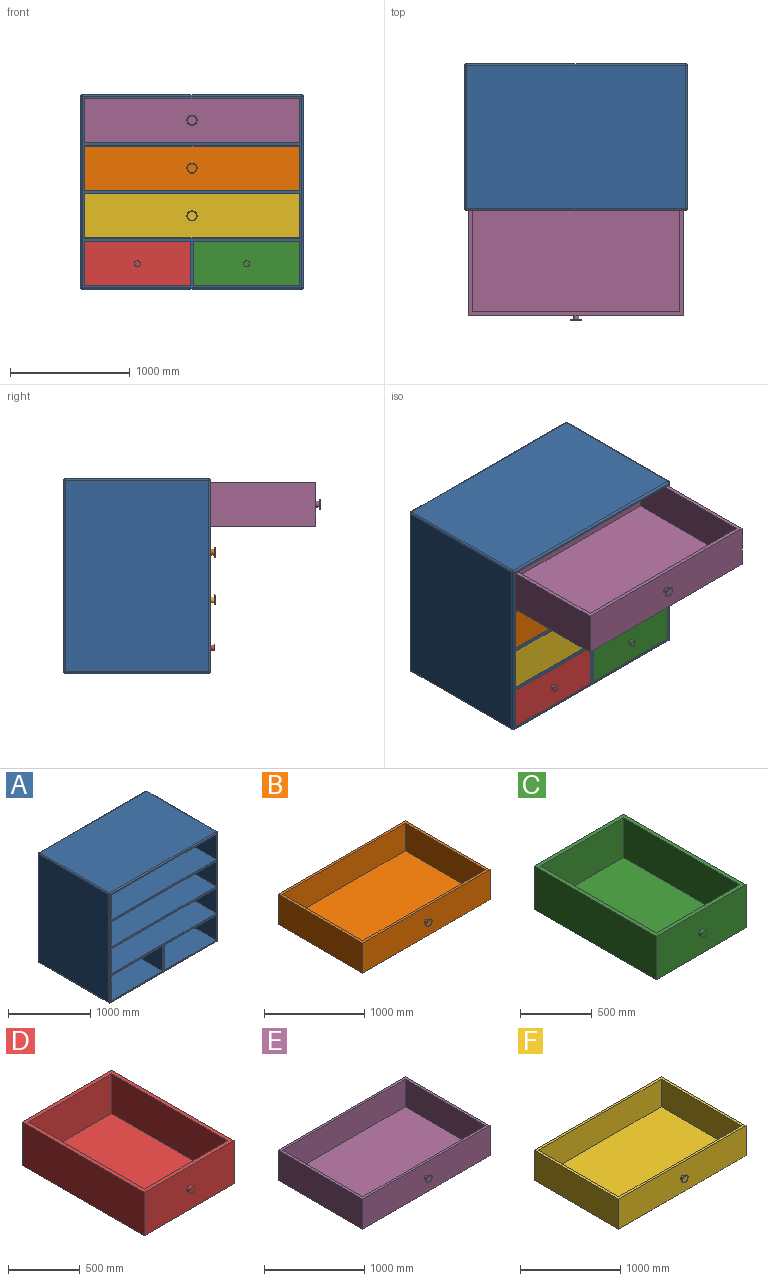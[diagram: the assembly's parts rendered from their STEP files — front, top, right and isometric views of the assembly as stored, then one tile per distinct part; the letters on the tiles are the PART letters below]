
ASSEMBLY  parts=6 mates=5
PART A: 51 faces, bbox 1860x1230x1630 mm
  f0: plane 885x370mm, normal (0,-1,0), area 327450mm2, adj f15,f21,f28,f29
  f1: plane 1200x885mm, normal (0,0,1), area 1062000mm2, adj f3,f12,f20,f30
  f2: plane 1200x885mm, normal (0,0,-1), area 1062000mm2, adj f3,f12,f20,f30
  f3: plane 1200x370mm, normal (-1,0,0), area 444000mm2, adj f1,f2,f12,f20
  f4: plane 1200x370mm, normal (1,0,0), area 444000mm2, adj f5,f12,f23,f27
  f5: plane 1800x370mm, normal (0,-1,0), area 666000mm2, adj f4,f10,f23,f27
  f6: plane 1200x370mm, normal (1,0,0), area 444000mm2, adj f7,f12,f14,f25
  f7: plane 1800x370mm, normal (0,-1,0), area 666000mm2, adj f6,f14,f17,f25
  f8: plane 1200x370mm, normal (-1,0,0), area 444000mm2, adj f11,f12,f24,f26
  f9: plane 1200x370mm, normal (1,0,0), area 444000mm2, adj f11,f12,f24,f26
  f10: plane 1200x370mm, normal (-1,0,0), area 444000mm2, adj f5,f12,f23,f27
  f11: plane 1800x370mm, normal (0,-1,0), area 666000mm2, adj f8,f9,f24,f26
  f12: plane 1830x1600mm, normal (0,-1,0), area 275100mm2, adj f1,f2,f3,f4,f6,f8,f9,f10
  f13: plane 1830x1200mm, normal (0,0,1), area 2196000mm2, adj f31,f35,f36,f37
  f14: plane 1800x1200mm, normal (0,0,-1), area 2160000mm2, adj f6,f7,f12,f17
  f15: plane 1200x370mm, normal (1,0,0), area 444000mm2, adj f0,f12,f21,f28
  f16: plane 1600x1200mm, normal (-1,0,0), area 1920000mm2, adj f37,f38,f46,f47
  f17: plane 1200x370mm, normal (-1,0,0), area 444000mm2, adj f7,f12,f14,f25
  f18: plane 1600x1200mm, normal (1,0,0), area 1920000mm2, adj f34,f35,f44,f45
  f19: plane 1830x1600mm, normal (0,1,0), area 2928000mm2, adj f36,f45,f46,f50
  f20: plane 885x370mm, normal (0,-1,0), area 327450mm2, adj f1,f2,f3,f30
  f21: plane 1200x885mm, normal (0,0,1), area 1062000mm2, adj f0,f12,f15,f29
  f22: plane 1830x1200mm, normal (0,0,-1), area 2196000mm2, adj f39,f44,f47,f50
  f23: plane 1800x1200mm, normal (0,0,-1), area 2160000mm2, adj f4,f5,f10,f12
  f24: plane 1800x1200mm, normal (0,0,1), area 2160000mm2, adj f8,f9,f11,f12
  f25: plane 1800x1200mm, normal (0,0,1), area 2160000mm2, adj f6,f7,f12,f17
  f26: plane 1800x1200mm, normal (0,0,-1), area 2160000mm2, adj f8,f9,f11,f12
  f27: plane 1800x1200mm, normal (0,0,1), area 2160000mm2, adj f4,f5,f10,f12
  f28: plane 1200x885mm, normal (0,0,-1), area 1062000mm2, adj f0,f12,f15,f29
  f29: plane 1200x370mm, normal (-1,0,0), area 444000mm2, adj f0,f12,f21,f28
  f30: plane 1200x370mm, normal (1,0,0), area 444000mm2, adj f1,f2,f12,f20
  f31: cylinder r=15mm len=1830mm, axis (-1,0,0), area 43118.4mm2, adj f12,f13,f32,f33
  f32: sphere r=15mm, area 353.4mm2, adj f31,f34,f35
  f33: sphere r=15mm, area 353.4mm2, adj f31,f37,f38
  f34: cylinder r=15mm len=1600mm, axis (0,0,-1), area 37699.1mm2, adj f12,f18,f32,f40
  f35: cylinder r=15mm len=1200mm, axis (0,-1,0), area 28274.3mm2, adj f13,f18,f32,f41
  f36: cylinder r=15mm len=1830mm, axis (-1,0,0), area 43118.4mm2, adj f13,f19,f41,f42
  f37: cylinder r=15mm len=1200mm, axis (0,-1,0), area 28274.3mm2, adj f13,f16,f33,f42
  f38: cylinder r=15mm len=1600mm, axis (0,0,-1), area 37699.1mm2, adj f12,f16,f33,f43
  f39: cylinder r=15mm len=1830mm, axis (1,0,0), area 43118.4mm2, adj f12,f22,f40,f43
  f40: sphere r=15mm, area 353.4mm2, adj f34,f39,f44
  f41: sphere r=15mm, area 353.4mm2, adj f35,f36,f45
  f42: sphere r=15mm, area 353.4mm2, adj f36,f37,f46
  f43: sphere r=15mm, area 353.4mm2, adj f38,f39,f47
  f44: cylinder r=15mm len=1200mm, axis (0,-1,0), area 28274.3mm2, adj f18,f22,f40,f48
  f45: cylinder r=15mm len=1600mm, axis (0,0,-1), area 37699.1mm2, adj f18,f19,f41,f48
  f46: cylinder r=15mm len=1600mm, axis (0,0,-1), area 37699.1mm2, adj f16,f19,f42,f49
  f47: cylinder r=15mm len=1200mm, axis (0,-1,0), area 28274.3mm2, adj f16,f22,f43,f49
  f48: sphere r=15mm, area 353.4mm2, adj f44,f45,f50
  f49: sphere r=15mm, area 353.4mm2, adj f46,f47,f50
  f50: cylinder r=15mm len=1830mm, axis (-1,0,0), area 43118.4mm2, adj f19,f22,f48,f49
PART B: 15 faces, bbox 1798x1240x368 mm
  f0: plane 1738x1140mm, normal (0,0,1), area 1981320mm2, adj f1,f2,f3,f10
  f1: plane 1140x338mm, normal (1,0,0), area 385320mm2, adj f0,f3,f5,f10
  f2: plane 1140x338mm, normal (-1,0,0), area 385320mm2, adj f0,f3,f5,f10
  f3: plane 1738x338mm, normal (0,-1,0), area 587444mm2, adj f0,f1,f2,f5
  f4: plane 1200x368mm, normal (1,0,0), area 441600mm2, adj f5,f7,f8,f9
  f5: plane 1798x1200mm, normal (0,0,1), area 176280mm2, adj f1,f2,f3,f4,f6,f8,f9,f10
  f6: plane 1200x368mm, normal (-1,0,0), area 441600mm2, adj f5,f7,f8,f9
  f7: plane 1798x1200mm, normal (0,0,-1), area 2157600mm2, adj f4,f6,f8,f9
  f8: plane 1798x368mm, normal (0,1,0), area 661664mm2, adj f4,f5,f6,f7
  f9: plane 1798x368mm, normal (0,-1,0), area 659700.5mm2, adj f4,f5,f6,f7,f11
  f10: plane 1738x338mm, normal (0,1,0), area 587444mm2, adj f0,f1,f2,f5
  f11: cylinder r=25mm len=50mm, axis (0,1,0), area 4712.4mm2, adj f9,f13
  f12: plane 75.11x75.11mm, normal (0,-1,0), area 4431.2mm2, adj f14
  f13: plane 75.11x75.11mm, normal (0,1,0), area 2467.7mm2, adj f11,f14
  f14: torus R=37.56mm, axis (0,-1,0), area 4020.8mm2, adj f12,f13
PART C: 13 faces, bbox 883x1230x368 mm
  f0: plane 1140x823mm, normal (0,0,1), area 938220mm2, adj f1,f8,f9,f10
  f1: plane 1140x338mm, normal (-1,0,0), area 385320mm2, adj f0,f7,f8,f10
  f2: plane 883x368mm, normal (0,-1,0), area 322980.5mm2, adj f3,f5,f6,f7,f11
  f3: plane 1200x368mm, normal (-1,0,0), area 441600mm2, adj f2,f4,f6,f7
  f4: plane 883x368mm, normal (0,1,0), area 324944mm2, adj f3,f5,f6,f7
  f5: plane 1200x368mm, normal (1,0,0), area 441600mm2, adj f2,f4,f6,f7
  f6: plane 1200x883mm, normal (0,0,-1), area 1059600mm2, adj f2,f3,f4,f5
  f7: plane 1200x883mm, normal (0,0,1), area 121380mm2, adj f1,f2,f3,f4,f5,f8,f9,f10
  f8: plane 823x338mm, normal (0,-1,0), area 278174mm2, adj f0,f1,f7,f9
  f9: plane 1140x338mm, normal (1,0,0), area 385320mm2, adj f0,f7,f8,f10
  f10: plane 823x338mm, normal (0,1,0), area 278174mm2, adj f0,f1,f7,f9
  f11: cylinder r=25mm len=50mm, axis (0,1,0), area 4712.4mm2, adj f2,f12
  f12: plane 50x50mm, normal (0,-1,0), area 1963.5mm2, adj f11
PART D: 13 faces, bbox 883x1230x368 mm
  f0: plane 1140x823mm, normal (0,0,1), area 938220mm2, adj f1,f8,f9,f10
  f1: plane 1140x338mm, normal (1,0,0), area 385320mm2, adj f0,f7,f8,f10
  f2: plane 883x368mm, normal (0,-1,0), area 322980.5mm2, adj f3,f5,f6,f7,f11
  f3: plane 1200x368mm, normal (1,0,0), area 441600mm2, adj f2,f4,f6,f7
  f4: plane 883x368mm, normal (0,1,0), area 324944mm2, adj f3,f5,f6,f7
  f5: plane 1200x368mm, normal (-1,0,0), area 441600mm2, adj f2,f4,f6,f7
  f6: plane 1200x883mm, normal (0,0,-1), area 1059600mm2, adj f2,f3,f4,f5
  f7: plane 1200x883mm, normal (0,0,1), area 121380mm2, adj f1,f2,f3,f4,f5,f8,f9,f10
  f8: plane 823x338mm, normal (0,-1,0), area 278174mm2, adj f0,f1,f7,f9
  f9: plane 1140x338mm, normal (-1,0,0), area 385320mm2, adj f0,f7,f8,f10
  f10: plane 823x338mm, normal (0,1,0), area 278174mm2, adj f0,f1,f7,f9
  f11: cylinder r=25mm len=50mm, axis (0,1,0), area 4712.4mm2, adj f2,f12
  f12: plane 50x50mm, normal (0,-1,0), area 1963.5mm2, adj f11
PART E: 15 faces, bbox 1798x1240x368 mm
  f0: plane 1738x1140mm, normal (0,0,1), area 1981320mm2, adj f1,f2,f3,f10
  f1: plane 1140x338mm, normal (1,0,0), area 385320mm2, adj f0,f3,f5,f10
  f2: plane 1140x338mm, normal (-1,0,0), area 385320mm2, adj f0,f3,f5,f10
  f3: plane 1738x338mm, normal (0,-1,0), area 587444mm2, adj f0,f1,f2,f5
  f4: plane 1200x368mm, normal (1,0,0), area 441600mm2, adj f5,f7,f8,f9
  f5: plane 1798x1200mm, normal (0,0,1), area 176280mm2, adj f1,f2,f3,f4,f6,f8,f9,f10
  f6: plane 1200x368mm, normal (-1,0,0), area 441600mm2, adj f5,f7,f8,f9
  f7: plane 1798x1200mm, normal (0,0,-1), area 2157600mm2, adj f4,f6,f8,f9
  f8: plane 1798x368mm, normal (0,1,0), area 661664mm2, adj f4,f5,f6,f7
  f9: plane 1798x368mm, normal (0,-1,0), area 659700.5mm2, adj f4,f5,f6,f7,f11
  f10: plane 1738x338mm, normal (0,1,0), area 587444mm2, adj f0,f1,f2,f5
  f11: cylinder r=25mm len=50mm, axis (0,1,0), area 4712.4mm2, adj f9,f13
  f12: plane 75.11x75.11mm, normal (0,-1,0), area 4431.2mm2, adj f14
  f13: plane 75.11x75.11mm, normal (0,1,0), area 2467.7mm2, adj f11,f14
  f14: torus R=37.56mm, axis (0,-1,0), area 4020.8mm2, adj f12,f13
PART F: 15 faces, bbox 1798x1240x368 mm
  f0: plane 1738x1140mm, normal (0,0,1), area 1981320mm2, adj f1,f2,f3,f10
  f1: plane 1140x338mm, normal (1,0,0), area 385320mm2, adj f0,f3,f5,f10
  f2: plane 1140x338mm, normal (-1,0,0), area 385320mm2, adj f0,f3,f5,f10
  f3: plane 1738x338mm, normal (0,-1,0), area 587444mm2, adj f0,f1,f2,f5
  f4: plane 1200x368mm, normal (1,0,0), area 441600mm2, adj f5,f7,f8,f9
  f5: plane 1798x1200mm, normal (0,0,1), area 176280mm2, adj f1,f2,f3,f4,f6,f8,f9,f10
  f6: plane 1200x368mm, normal (-1,0,0), area 441600mm2, adj f5,f7,f8,f9
  f7: plane 1798x1200mm, normal (0,0,-1), area 2157600mm2, adj f4,f6,f8,f9
  f8: plane 1798x368mm, normal (0,1,0), area 661664mm2, adj f4,f5,f6,f7
  f9: plane 1798x368mm, normal (0,-1,0), area 659700.5mm2, adj f4,f5,f6,f7,f11
  f10: plane 1738x338mm, normal (0,1,0), area 587444mm2, adj f0,f1,f2,f5
  f11: cylinder r=25mm len=50mm, axis (0,1,0), area 4712.4mm2, adj f9,f13
  f12: plane 75.11x75.11mm, normal (0,-1,0), area 4431.2mm2, adj f14
  f13: plane 75.11x75.11mm, normal (0,1,0), area 2467.7mm2, adj f11,f14
  f14: torus R=37.56mm, axis (0,-1,0), area 4020.8mm2, adj f12,f13
PLACE A t=(-578.78,0,418.87)mm fixed
PLACE B t=(-578.78,0,418.87)mm
PLACE C t=(-578.78,0,419.87)mm
PLACE D t=(-578.78,0,419.87)mm
PLACE E t=(-578.78,-878.08,418.87)mm
PLACE F t=(-578.78,0,418.87)mm
MATE slider A.f0 <-> D.f11  axis (0,-1,0) through (-1036.28,600,-966.13)mm
MATE slider A.f5 <-> F.f11  axis (0,-1,0) through (-578.78,600,-566.13)mm
MATE slider A.f11 <-> B.f11  axis (0,-1,0) through (-578.78,600,-166.13)mm
MATE slider E.f11 <-> A.f7  axis (0,1,0) through (-578.78,-278.08,233.87)mm
MATE slider A.f20 <-> C.f11  axis (0,-1,0) through (-121.28,600,-966.13)mm
